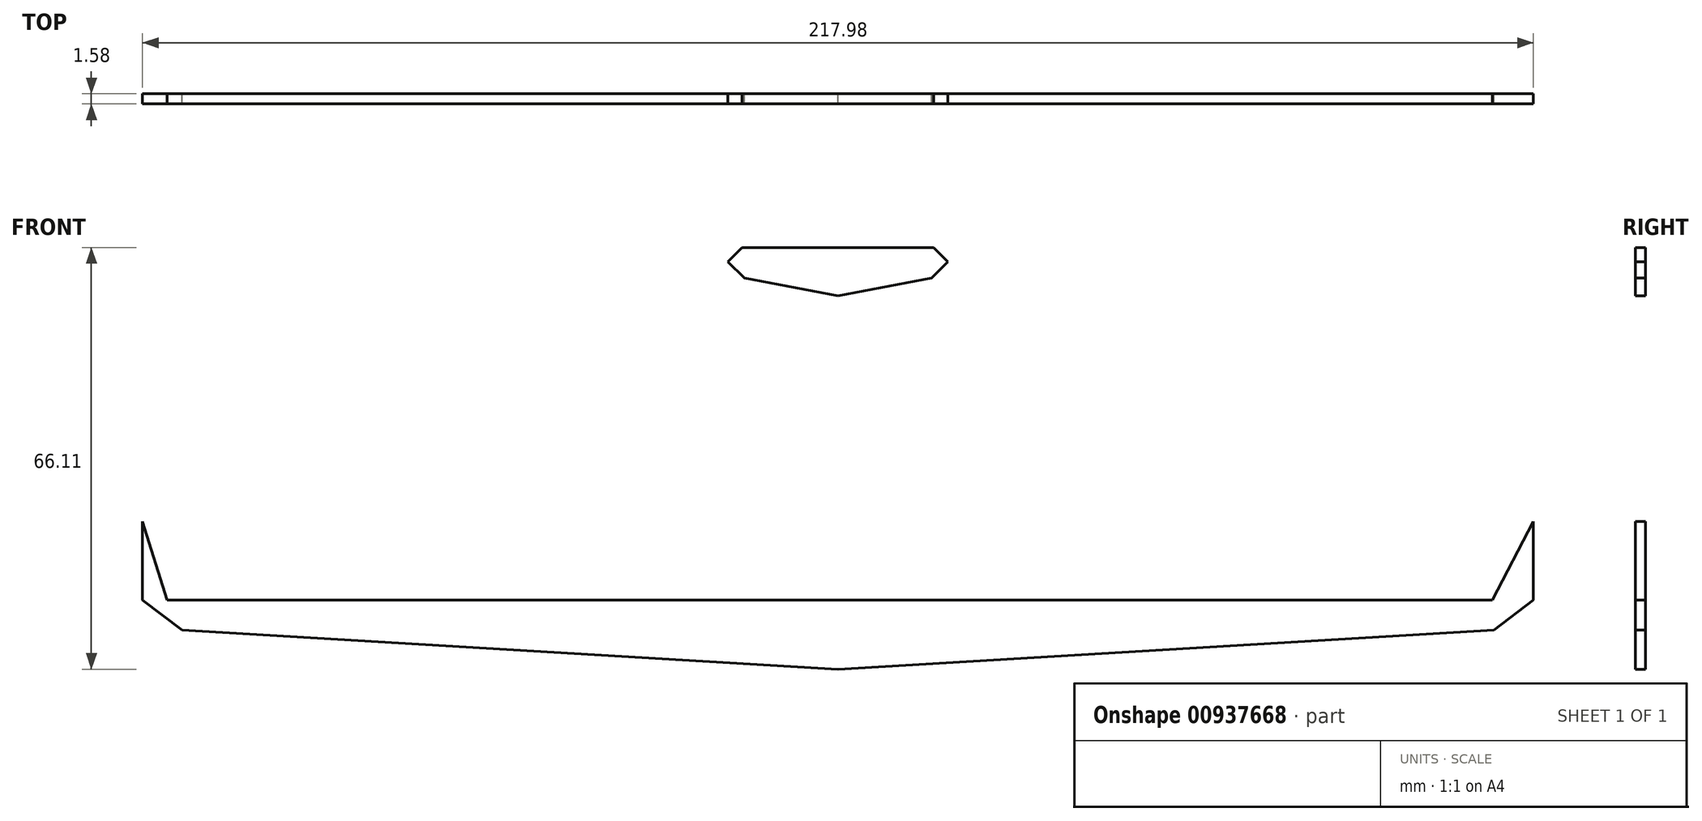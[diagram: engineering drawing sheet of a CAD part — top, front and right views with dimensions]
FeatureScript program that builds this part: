
annotation { "Feature Type Name" : "Feature", "Feature Type Description" : "" }
export const myFeature = defineFeature(function(context is Context, id is Id, definition is map)
    precondition{}
    {
        {
            var Q0;
            Q0=qCreatedBy(makeId("Front.planeOp"),FACE);
            var sketch = newSketch(context, id + "F0", { "sketchPlane" : qUnion([Q0])});
            skLineSegment(sketch, "E0.bottom", {"start": v(114.3, 50.8) * mm, "end": v(-114.3, 50.8) * mm, "construction": true});
            skLineSegment(sketch, "E0.top", {"start": v(114.3, -50.8) * mm, "end": v(-114.3, -50.8) * mm, "construction": true});
            skLineSegment(sketch, "E0.left", {"start": v(114.3, 50.8) * mm, "end": v(114.3, -50.8) * mm, "construction": true});
            skLineSegment(sketch, "E0.right", {"start": v(-114.3, 50.8) * mm, "end": v(-114.3, -50.8) * mm, "construction": true});
            skPoint(sketch, "E0.middle", {"position": v(0, 0) * mm});
            skLineSegment(sketch, "E1", {"start": v(0, -51.28) * mm, "end": v(0, 50.8) * mm, "construction": true});
            skLineSegment(sketch, "E2.MirrorCS", {"start": v(0, -23.13) * mm, "end": v(102.8, -17) * mm});
            skLineSegment(sketch, "E3.MirrorCS", {"start": v(49.54, -19.78) * mm, "end": v(49.54, -15.77) * mm});
            skLineSegment(sketch, "E4.MirrorCS", {"start": v(31.41, -19.78) * mm, "end": v(31.41, -15.77) * mm});
            skLineSegment(sketch, "E5.MirrorCS", {"start": v(49.54, -19.78) * mm, "end": v(31.41, -19.78) * mm});
            skLineSegment(sketch, "E6.MirrorCS", {"start": v(49.54, -15.77) * mm, "end": v(31.41, -15.77) * mm});
            skLineSegment(sketch, "E7", {"start": v(0, 35.37) * mm, "end": v(-14.68, 38.17) * mm});
            skLineSegment(sketch, "E8", {"start": v(-14.68, 38.17) * mm, "end": v(-17.25, 40.74) * mm});
            skLineSegment(sketch, "E9", {"start": v(-17.25, 40.74) * mm, "end": v(-15.01, 42.98) * mm});
            skLineSegment(sketch, "E10", {"start": v(-15.01, 42.98) * mm, "end": v(0, 42.98) * mm});
            skLineSegment(sketch, "E11", {"start": v(0, 40.74) * mm, "end": v(-15.97, 42.02) * mm});
            skPoint(sketch, "E11.endSnap0", {"position": v(-15.97, 39.46) * mm});
            skLineSegment(sketch, "E12.MirrorCS", {"start": v(17.25, 40.74) * mm, "end": v(15.01, 42.98) * mm});
            skLineSegment(sketch, "E13.MirrorCS", {"start": v(14.68, 38.17) * mm, "end": v(17.25, 40.74) * mm});
            skLineSegment(sketch, "E14.MirrorCS", {"start": v(0, 35.37) * mm, "end": v(14.68, 38.17) * mm});
            skLineSegment(sketch, "E15.MirrorCS", {"start": v(0, 40.74) * mm, "end": v(15.97, 42.02) * mm});
            skLineSegment(sketch, "E16.MirrorCS", {"start": v(15.01, 42.98) * mm, "end": v(0, 42.98) * mm});
            skLineSegment(sketch, "E17.bottom", {"start": v(-30.52, 50.8) * mm, "end": v(30.52, 50.8) * mm});
            skLineSegment(sketch, "E17.top", {"start": v(-30.52, -50.8) * mm, "end": v(30.52, -50.8) * mm});
            skLineSegment(sketch, "E18", {"start": v(0, -12.32) * mm, "end": v(109, -12.32) * mm});
            skLineSegment(sketch, "E19", {"start": v(109, -12.32) * mm, "end": v(102.8, -17) * mm});
            skLineSegment(sketch, "E20", {"start": v(109, -12.32) * mm, "end": v(109, 0) * mm});
            skLineSegment(sketch, "E21.MirrorCS", {"start": v(-109, -12.32) * mm, "end": v(-109, 0) * mm});
            skLineSegment(sketch, "E22.MirrorCS", {"start": v(-109, -12.32) * mm, "end": v(-102.8, -17) * mm});
            skLineSegment(sketch, "E23.MirrorCS", {"start": v(0, -12.32) * mm, "end": v(-109, -12.32) * mm});
            skLineSegment(sketch, "E24.MirrorCS", {"start": v(0, -23.13) * mm, "end": v(-102.8, -17) * mm});
            skLineSegment(sketch, "E25.MirrorCS", {"start": v(-31.41, -19.78) * mm, "end": v(-31.41, -15.77) * mm});
            skLineSegment(sketch, "E26.MirrorCS", {"start": v(-49.54, -15.77) * mm, "end": v(-31.41, -15.77) * mm});
            skLineSegment(sketch, "E27.MirrorCS", {"start": v(-49.54, -19.78) * mm, "end": v(-31.41, -19.78) * mm});
            skLineSegment(sketch, "E28.MirrorCS", {"start": v(-49.54, -19.78) * mm, "end": v(-49.54, -15.77) * mm});
            skLineSegment(sketch, "E29", {"start": v(-109, 0) * mm, "end": v(-105.14, -12.32) * mm});
            skLineSegment(sketch, "E30.MirrorCS", {"start": v(-169.42, -104.2) * mm, "end": v(-227.52, -20.26) * mm, "construction": true});
            skLineSegment(sketch, "E31", {"start": v(109, 0) * mm, "end": v(102.59, -12.32) * mm});
            skSolve(sketch);
        }
        {
            var Q0;
            Q0=makeQuery(id+"F0.imprint","IMPRINT",FACE,{"disambiguationData":[TD([[makeQuery(id+"F0.imprint","IMPRINT",EDGE,{"derivedFrom":sQuery(id+"F0.wireOp",EDGE,"E25.MirrorCS")}),1.0]])]});
            var Q1;
            Q1=makeQuery(id+"F0.imprint","IMPRINT",FACE,{"disambiguationData":[TD([[makeQuery(id+"F0.imprint","IMPRINT",EDGE,{"derivedFrom":sQuery(id+"F0.wireOp",EDGE,"E2.MirrorCS")}),1.0]])]});
            var Q2;
            Q2=makeQuery(id+"F0.imprint","IMPRINT",FACE,{"disambiguationData":[TD([[makeQuery(id+"F0.imprint","IMPRINT",EDGE,{"derivedFrom":sQuery(id+"F0.wireOp",EDGE,"E3.MirrorCS")}),1.0]])]});
            var Q3;
            Q3=makeQuery(id+"F0.imprint","IMPRINT",FACE,{"disambiguationData":[TD([[makeQuery(id+"F0.imprint","IMPRINT",EDGE,{"derivedFrom":sQuery(id+"F0.wireOp",EDGE,"E7")}),-1.0]])]});
            var Q4;
            {var subQ4=sQuery(id+"F0.wireOp",EDGE,"E10");Q4=makeQuery(id+"F0.imprint","IMPRINT",FACE,{"disambiguationData":[TD([[makeQuery(id+"F0.imprint","IMPRINT",EDGE,{"derivedFrom":subQ4}),-1.0]])]});}
            var Q5;
            {var subQ0=sQuery(id+"F0.wireOp",EDGE,"E21.MirrorCS");Q5=makeQuery(id+"F0.imprint","IMPRINT",FACE,{"disambiguationData":[TD([[makeQuery(id+"F0.imprint","IMPRINT",EDGE,{"derivedFrom":subQ0}),-1.0]])]});}
            var Q6;
            {var subQ0=sQuery(id+"F0.wireOp",EDGE,"E20");Q6=makeQuery(id+"F0.imprint","IMPRINT",FACE,{"disambiguationData":[TD([[makeQuery(id+"F0.imprint","IMPRINT",EDGE,{"derivedFrom":subQ0}),1.0]])]});}
            extrude(context, id + "F1", {"entities" : qUnion([Q0, Q1, Q2, Q3, Q4, Q5, Q6]), "endBound" : BoundingType.SYMMETRIC, "depth" : 1.59 * mm, "offsetDistance" : 25.4 * mm});
        }
    });
